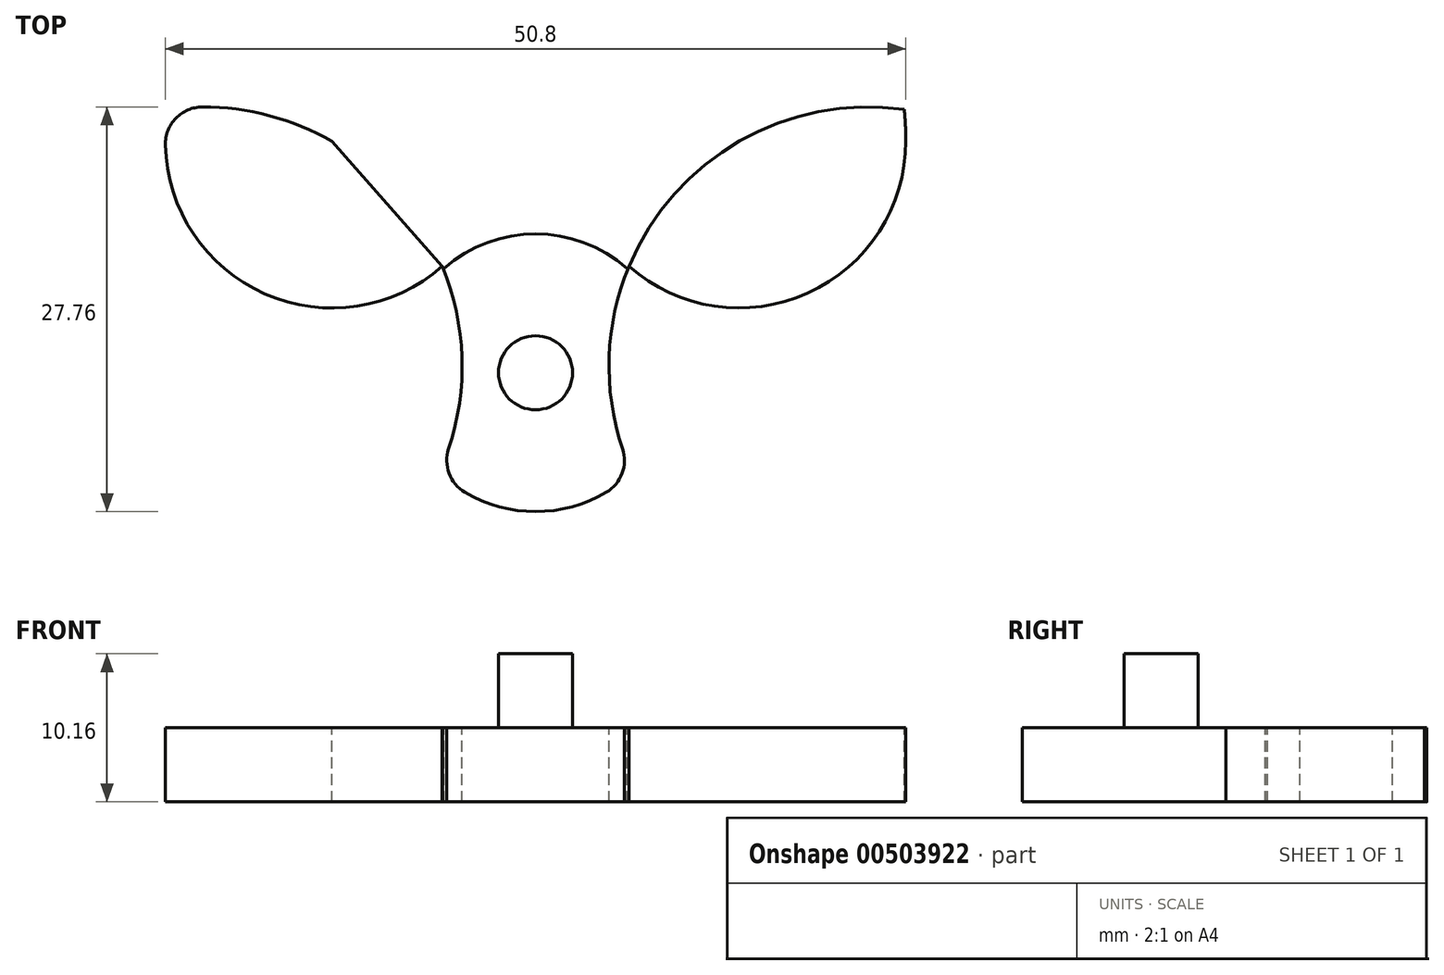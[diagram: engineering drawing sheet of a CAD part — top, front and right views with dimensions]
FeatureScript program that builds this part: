
annotation { "Feature Type Name" : "Feature", "Feature Type Description" : "" }
export const myFeature = defineFeature(function(context is Context, id is Id, definition is map)
    precondition{}
    {
        {
            var Q0;
            Q0=qCreatedBy(makeId("Top.planeOp"),FACE);
            var sketch = newSketch(context, id + "F0", { "sketchPlane" : qUnion([Q0])});
            skCircle(sketch, "E0", {"center": v(0, 0) * mm, "radius": 25.4 * mm});
            skSolve(sketch);
        }
        {
            var Q0;
            Q0 = qSketchRegion(id + "F0", true);
            extrude(context, id + "F1", {"entities" : qUnion([Q0]), "depth" : 5.08 * mm});
        }
        {
            var Q0;
            Q0=makeQuery(id+"F1.opExtrude","CAP_FACE",FACE,{"disambiguationData":[OSD([sQuery(id+"F0.wireOp",EDGE,"E0")])],"isStart":false});
            var sketch = newSketch(context, id + "F2", { "sketchPlane" : qUnion([Q0])});
            skCircle(sketch, "E1", {"center": v(0, -15.88) * mm, "radius": 9.53 * mm});
            skCircle(sketch, "E2", {"center": v(13.97, 0) * mm, "radius": 11.43 * mm});
            skCircle(sketch, "E3", {"center": v(-13.97, 0) * mm, "radius": 11.43 * mm});
            skLineSegment(sketch, "E4", {"start": v(13.97, 0) * mm, "end": v(0, -15.88) * mm});
            skLineSegment(sketch, "E5", {"start": v(0, -15.88) * mm, "end": v(-7.4, -24.3) * mm});
            skLineSegment(sketch, "E6", {"start": v(-13.97, 0) * mm, "end": v(0, -15.88) * mm});
            skLineSegment(sketch, "E7", {"start": v(0, -15.88) * mm, "end": v(7.4, -24.3) * mm});
            skCircle(sketch, "E8", {"center": v(-22.82, -15.42) * mm, "radius": 17.78 * mm});
            skPoint(sketch, "E8.third.point", {"position": v(-40.58, -16.22) * mm});
            skCircle(sketch, "E9", {"center": v(22.82, -15.42) * mm, "radius": 17.78 * mm});
            skPoint(sketch, "E9.third.point", {"position": v(40.2, -11.66) * mm});
            skSolve(sketch);
        }
        {
            var Q0;
            {var subQ0=sQuery(id+"F2.wireOp",EDGE,"E8");var subQ1=sQuery(id+"F2.wireOp",EDGE,"E1");var subQ2=makeQuery(id+"F2.imprint","INTERSECT",VERTEX,{"disambiguationData":[OD(0.0)],"derivedFrom":[subQ1,subQ0]});Q0=makeQuery(id+"F2.imprint","IMPRINT",FACE,{"disambiguationData":[TD([[makeQuery(id+"F2.imprint","IMPRINT",EDGE,{"disambiguationData":[TD([[subQ2,-1.0]])],"derivedFrom":subQ1}),-1.0]])]});}
            var Q1;
            {var subQ0=sQuery(id+"F2.wireOp",EDGE,"E6");var subQ1=sQuery(id+"F2.wireOp",EDGE,"E3");var subQ2=makeQuery(id+"F2.imprint","INTERSECT",VERTEX,{"derivedFrom":[subQ1,subQ0]});Q1=makeQuery(id+"F2.imprint","IMPRINT",FACE,{"disambiguationData":[TD([[makeQuery(id+"F2.imprint","IMPRINT",EDGE,{"disambiguationData":[TD([[subQ2,-1.0]])],"derivedFrom":subQ1}),1.0]])]});}
            var Q2;
            {var subQ0=sQuery(id+"F2.wireOp",EDGE,"E8");var subQ1=sQuery(id+"F2.wireOp",EDGE,"E3");var subQ2=makeQuery(id+"F2.imprint","INTERSECT",VERTEX,{"disambiguationData":[OD(0.0)],"derivedFrom":[subQ1,subQ0]});Q2=makeQuery(id+"F2.imprint","IMPRINT",FACE,{"disambiguationData":[TD([[makeQuery(id+"F2.imprint","IMPRINT",EDGE,{"disambiguationData":[TD([[subQ2,-1.0]])],"derivedFrom":subQ1}),1.0]])]});}
            var Q3;
            {var subQ0=sQuery(id+"F2.wireOp",EDGE,"E8");var subQ1=sQuery(id+"F2.wireOp",EDGE,"E1");var subQ2=makeQuery(id+"F2.imprint","INTERSECT",VERTEX,{"disambiguationData":[OD(0.0)],"derivedFrom":[subQ1,subQ0]});Q3=makeQuery(id+"F2.imprint","IMPRINT",FACE,{"disambiguationData":[TD([[makeQuery(id+"F2.imprint","IMPRINT",EDGE,{"disambiguationData":[TD([[subQ2,-1.0]])],"derivedFrom":subQ1}),1.0]])]});}
            var Q4;
            {var subQ0=sQuery(id+"F2.wireOp",EDGE,"E5");var subQ1=sQuery(id+"F2.wireOp",EDGE,"E1");var subQ2=makeQuery(id+"F2.imprint","INTERSECT",VERTEX,{"derivedFrom":[subQ1,subQ0]});Q4=makeQuery(id+"F2.imprint","IMPRINT",FACE,{"disambiguationData":[TD([[makeQuery(id+"F2.imprint","IMPRINT",EDGE,{"disambiguationData":[TD([[subQ2,-1.0]])],"derivedFrom":subQ1}),-1.0]])]});}
            var Q5;
            {var subQ0=sQuery(id+"F2.wireOp",EDGE,"E7");var subQ1=sQuery(id+"F2.wireOp",EDGE,"E1");var subQ2=makeQuery(id+"F2.imprint","INTERSECT",VERTEX,{"derivedFrom":[subQ1,subQ0]});Q5=makeQuery(id+"F2.imprint","IMPRINT",FACE,{"disambiguationData":[TD([[makeQuery(id+"F2.imprint","IMPRINT",EDGE,{"disambiguationData":[TD([[subQ2,1.0]])],"derivedFrom":subQ1}),-1.0]])]});}
            var Q6;
            {var subQ0=sQuery(id+"F2.wireOp",EDGE,"E9");var subQ1=sQuery(id+"F2.wireOp",EDGE,"E1");var subQ2=makeQuery(id+"F2.imprint","INTERSECT",VERTEX,{"disambiguationData":[OD(0.0)],"derivedFrom":[subQ1,subQ0]});Q6=makeQuery(id+"F2.imprint","IMPRINT",FACE,{"disambiguationData":[TD([[makeQuery(id+"F2.imprint","IMPRINT",EDGE,{"disambiguationData":[TD([[subQ2,1.0]])],"derivedFrom":subQ1}),-1.0]])]});}
            var Q7;
            {var subQ0=sQuery(id+"F2.wireOp",EDGE,"E9");var subQ1=sQuery(id+"F2.wireOp",EDGE,"E2");var subQ2=makeQuery(id+"F2.imprint","INTERSECT",VERTEX,{"disambiguationData":[OD(0.0)],"derivedFrom":[subQ1,subQ0]});Q7=makeQuery(id+"F2.imprint","IMPRINT",FACE,{"disambiguationData":[TD([[makeQuery(id+"F2.imprint","IMPRINT",EDGE,{"disambiguationData":[TD([[subQ2,1.0]])],"derivedFrom":subQ1}),1.0]])]});}
            var Q8;
            {var subQ0=sQuery(id+"F2.wireOp",EDGE,"E9");var subQ1=sQuery(id+"F2.wireOp",EDGE,"E1");var subQ2=makeQuery(id+"F2.imprint","INTERSECT",VERTEX,{"disambiguationData":[OD(0.0)],"derivedFrom":[subQ1,subQ0]});Q8=makeQuery(id+"F2.imprint","IMPRINT",FACE,{"disambiguationData":[TD([[makeQuery(id+"F2.imprint","IMPRINT",EDGE,{"disambiguationData":[TD([[subQ2,1.0]])],"derivedFrom":subQ1}),1.0]])]});}
            var Q9;
            {var subQ0=sQuery(id+"F2.wireOp",EDGE,"E9");var subQ1=sQuery(id+"F2.wireOp",EDGE,"E2");var subQ2=makeQuery(id+"F2.imprint","INTERSECT",VERTEX,{"disambiguationData":[OD(1.0)],"derivedFrom":[subQ1,subQ0]});Q9=makeQuery(id+"F2.imprint","IMPRINT",FACE,{"disambiguationData":[TD([[makeQuery(id+"F2.imprint","IMPRINT",EDGE,{"disambiguationData":[TD([[subQ2,-1.0]])],"derivedFrom":subQ1}),1.0]])]});}
            var Q10;
            {var subQ0=sQuery(id+"F2.wireOp",EDGE,"E8");var subQ1=sQuery(id+"F2.wireOp",EDGE,"E1");var subQ2=makeQuery(id+"F2.imprint","INTERSECT",VERTEX,{"disambiguationData":[OD(1.0)],"derivedFrom":[subQ1,subQ0]});Q10=makeQuery(id+"F2.imprint","IMPRINT",FACE,{"disambiguationData":[TD([[makeQuery(id+"F2.imprint","IMPRINT",EDGE,{"disambiguationData":[TD([[subQ2,-1.0]])],"derivedFrom":subQ1}),-1.0]])]});}
            var Q11;
            {var subQ0=sQuery(id+"F2.wireOp",EDGE,"E7");var subQ1=sQuery(id+"F2.wireOp",EDGE,"E1");var subQ2=makeQuery(id+"F2.imprint","INTERSECT",VERTEX,{"derivedFrom":[subQ1,subQ0]});Q11=makeQuery(id+"F2.imprint","IMPRINT",FACE,{"disambiguationData":[TD([[makeQuery(id+"F2.imprint","IMPRINT",EDGE,{"disambiguationData":[TD([[subQ2,-1.0]])],"derivedFrom":subQ1}),-1.0]])]});}
            var Q12;
            {var subQ0=sQuery(id+"F2.wireOp",EDGE,"E8");var subQ1=sQuery(id+"F2.wireOp",EDGE,"E3");var subQ2=makeQuery(id+"F2.imprint","INTERSECT",VERTEX,{"disambiguationData":[OD(0.0)],"derivedFrom":[subQ1,subQ0]});Q12=makeQuery(id+"F2.imprint","IMPRINT",FACE,{"disambiguationData":[TD([[makeQuery(id+"F2.imprint","IMPRINT",EDGE,{"disambiguationData":[TD([[subQ2,-1.0]])],"derivedFrom":subQ1}),-1.0]])]});}
            var Q13;
            {var subQ0=sQuery(id+"F2.wireOp",EDGE,"E9");var subQ1=sQuery(id+"F2.wireOp",EDGE,"E2");var subQ2=makeQuery(id+"F2.imprint","INTERSECT",VERTEX,{"disambiguationData":[OD(0.0)],"derivedFrom":[subQ1,subQ0]});Q13=makeQuery(id+"F2.imprint","IMPRINT",FACE,{"disambiguationData":[TD([[makeQuery(id+"F2.imprint","IMPRINT",EDGE,{"disambiguationData":[TD([[subQ2,1.0]])],"derivedFrom":subQ1}),-1.0]])]});}
            extrude(context, id + "F3", {"entities" : qUnion([Q0, Q1, Q2, Q3, Q4, Q5, Q6, Q7, Q8, Q9, Q10, Q11, Q12, Q13]), "operationType" : NewBodyOperationType.REMOVE, "oppositeDirection" : true, "depth" : 25.4 * mm});
        }
        {
            var Q0;
            Q0=makeQuery(id+"F3.boolean.opBoolean","COPY",EDGE,{"derivedFrom":makeQuery(id+"F3.opExtrude","SWEPT_EDGE",EDGE,{"disambiguationData":[OSD([sQuery(id+"F0.wireOp",EDGE,"E0"),sQuery(id+"F2.wireOp",EDGE,"E8")])]})});
            var Q1;
            Q1=makeQuery(id+"F3.boolean.opBoolean","COPY",EDGE,{"derivedFrom":makeQuery(id+"F3.opExtrude","SWEPT_EDGE",EDGE,{"disambiguationData":[OSD([sQuery(id+"F2.wireOp",EDGE,"E1"),sQuery(id+"F2.wireOp",EDGE,"E8")])]})});
            var Q2;
            Q2=makeQuery(id+"F3.boolean.opBoolean","COPY",EDGE,{"derivedFrom":makeQuery(id+"F3.opExtrude","SWEPT_EDGE",EDGE,{"disambiguationData":[OSD([sQuery(id+"F2.wireOp",EDGE,"E1"),sQuery(id+"F2.wireOp",EDGE,"E9")])]})});
            var Q3;
            Q3=makeQuery(id+"F3.boolean.opBoolean","COPY",EDGE,{"derivedFrom":makeQuery(id+"F3.opExtrude","SWEPT_EDGE",EDGE,{"disambiguationData":[OSD([sQuery(id+"F0.wireOp",EDGE,"E0"),sQuery(id+"F2.wireOp",EDGE,"E9")])]})});
            fillet(context, id + "F4", {"entities" : qUnion([Q0, Q1, Q2, Q3]), "radius" : 2.54 * mm, "tangentPropagation" : true, "allowEdgeOverflow" : false});
        }
        {
            var Q0;
            Q0=makeQuery(id+"F1.opExtrude","CAP_FACE",FACE,{"disambiguationData":[OSD([sQuery(id+"F0.wireOp",EDGE,"E0")])],"isStart":false});
            var sketch = newSketch(context, id + "F5", { "sketchPlane" : qUnion([Q0])});
            skCircle(sketch, "E10", {"center": v(0, 0) * mm, "radius": 2.54 * mm});
            skCircle(sketch, "E11", {"center": v(0, -18.95) * mm, "radius": 2.54 * mm});
            skSolve(sketch);
        }
        {
            var Q0;
            Q0=makeQuery(id+"F5.imprint","IMPRINT",FACE,{"disambiguationData":[TD([[makeQuery(id+"F5.imprint","IMPRINT",EDGE,{"derivedFrom":sQuery(id+"F5.wireOp",EDGE,"E10")}),1.0]])]});
            extrude(context, id + "F6", {"entities" : qUnion([Q0]), "operationType" : NewBodyOperationType.REMOVE, "oppositeDirection" : true, "depth" : 25.4 * mm});
        }
        {
            var Q0;
            Q0=makeQuery(id+"F1.opExtrude","CAP_FACE",FACE,{"disambiguationData":[OSD([sQuery(id+"F0.wireOp",EDGE,"E0")])],"isStart":false});
            var sketch = newSketch(context, id + "F7", { "sketchPlane" : qUnion([Q0])});
            skCircle(sketch, "E12", {"center": v(0, -15.88) * mm, "radius": 2.54 * mm});
            skLineSegment(sketch, "E13", {"start": v(0, -15.88) * mm, "end": v(0, 0) * mm});
            skSolve(sketch);
        }
        {
            var Q0;
            Q0=makeQuery(id+"F7.imprint","IMPRINT",FACE,{"disambiguationData":[TD([[makeQuery(id+"F7.imprint","IMPRINT",EDGE,{"derivedFrom":sQuery(id+"F7.wireOp",EDGE,"E12")}),1.0]])]});
            extrude(context, id + "F8", {"entities" : qUnion([Q0]), "operationType" : NewBodyOperationType.ADD, "depth" : 5.08 * mm});
        }
    });
